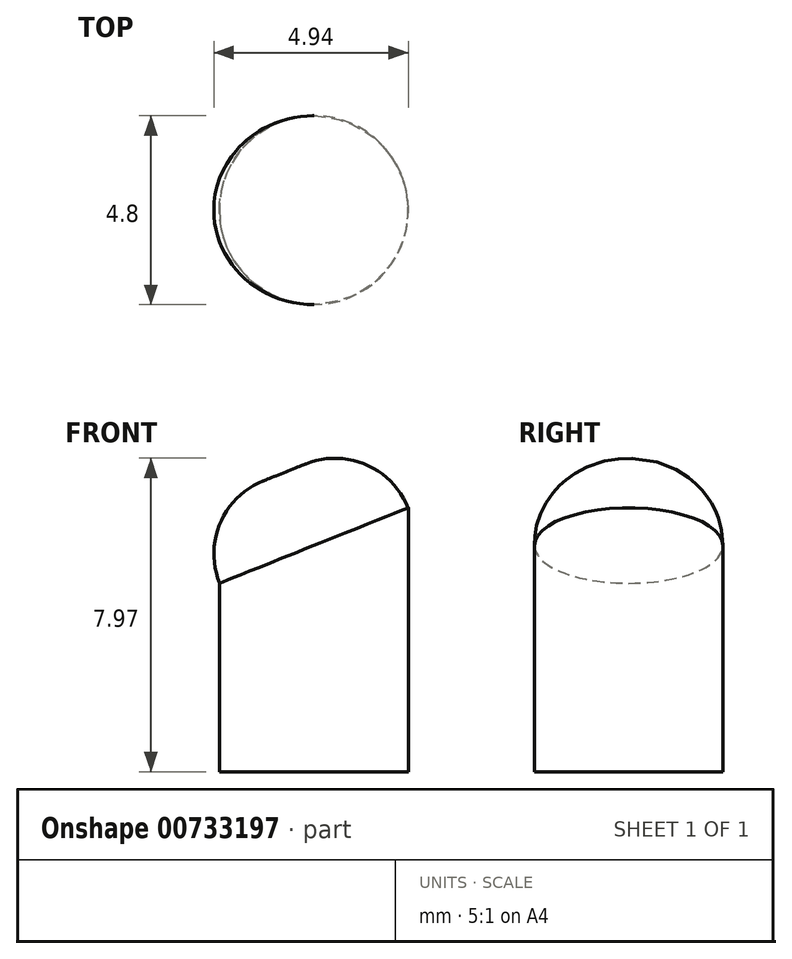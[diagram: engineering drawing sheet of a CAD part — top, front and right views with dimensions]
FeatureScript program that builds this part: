
annotation { "Feature Type Name" : "Feature", "Feature Type Description" : "" }
export const myFeature = defineFeature(function(context is Context, id is Id, definition is map)
    precondition{}
    {
        {
            var Q0;
            Q0=qCreatedBy(makeId("Top.planeOp"),FACE);
            var sketch = newSketch(context, id + "F0", { "sketchPlane" : qUnion([Q0])});
            skCircle(sketch, "E0", {"center": v(0, 0) * mm, "radius": 2.4 * mm});
            skSolve(sketch);
        }
        {
            var Q0;
            Q0=makeQuery(id+"F0.imprint","IMPRINT",FACE,{"disambiguationData":[TD([[makeQuery(id+"F0.imprint","IMPRINT",EDGE,{"derivedFrom":sQuery(id+"F0.wireOp",EDGE,"E0")}),1.0]])]});
            extrude(context, id + "F1", {"entities" : qUnion([Q0]), "depth" : 10 * mm, "offsetDistance" : 25 * mm});
        }
        {
            var Q0;
            Q0=qCreatedBy(makeId("Front.planeOp"),FACE);
            var sketch = newSketch(context, id + "F2", { "sketchPlane" : qUnion([Q0])});
            skLineSegment(sketch, "E1", {"start": v(-2.5, 4.75) * mm, "end": v(2.5, 6.75) * mm});
            skLineSegment(sketch, "E2", {"start": v(-2.5, 4.75) * mm, "end": v(-2.5, 10.5) * mm});
            skLineSegment(sketch, "E3", {"start": v(-2.5, 10.5) * mm, "end": v(2.5, 10.5) * mm});
            skLineSegment(sketch, "E4", {"start": v(2.5, 10.5) * mm, "end": v(2.5, 6.75) * mm});
            skSolve(sketch);
        }
        {
            var Q0;
            {var subQ2=sQuery(id+"F2.wireOp",EDGE,"LqtT72pM-FGjC-ddh8-95cH-kXxwAAOvpNlh");Q0=makeQuery(id+"F2.imprint","IMPRINT",FACE,{"disambiguationData":[TD([[makeQuery(id+"F2.imprint","IMPRINT",EDGE,{"derivedFrom":subQ2}),-1.0]])]});}
            var Q1;
            Q1=makeQuery(id+"F2.imprint","IMPRINT",FACE,{"disambiguationData":[TD([[makeQuery(id+"F2.imprint","IMPRINT",EDGE,{"derivedFrom":sQuery(id+"F2.wireOp",EDGE,"E1")}),1.0]])]});
            extrude(context, id + "F3", {"entities" : qUnion([Q0, Q1]), "operationType" : NewBodyOperationType.REMOVE, "endBound" : BoundingType.SYMMETRIC, "oppositeDirection" : true, "depth" : 8 * mm, "offsetDistance" : 25 * mm});
        }
        {
            var Q0;
            Q0=makeQuery(id+"F3.boolean.opBoolean","COPY",FACE,{"derivedFrom":makeQuery(id+"F3.opExtrude","SWEPT_FACE",FACE,{"disambiguationData":[OSD([sQuery(id+"F2.wireOp",EDGE,"E1")])]})});
            var sketch = newSketch(context, id + "F4", { "sketchPlane" : qUnion([Q0])});
            skEllipse(sketch, "E5", {"center": v(2.14, 0) * mm, "majorRadius": 2.6 * mm, "minorRadius": 2.4 * mm, "majorAxis": v(1, 0)});
            skSolve(sketch);
        }
        {
            var Q0;
            {var subQ0=sQuery(id+"F4.wireOp",EDGE,"E5");var subQ1=makeQuery(id+"F3.boolean.opBoolean","INTERSECT",EDGE,{"derivedFrom":[makeQuery(id+"F1.opExtrude","SWEPT_FACE",FACE,{"disambiguationData":[OSD([sQuery(id+"F0.wireOp",EDGE,"E0")])]}),makeQuery(id+"F3.opExtrude","SWEPT_FACE",FACE,{"disambiguationData":[OSD([sQuery(id+"F2.wireOp",EDGE,"E1")])]})]});var subQ2=makeQuery(id+"F4.imprint","INTERSECT",VERTEX,{"disambiguationData":[OD(0.0)],"derivedFrom":[subQ1,subQ0]});Q0=makeQuery(id+"F4.imprint","IMPRINT",FACE,{"disambiguationData":[TD([[makeQuery(id+"F4.imprint","IMPRINT",EDGE,{"disambiguationData":[TD([[subQ2,-1.0]])],"derivedFrom":subQ1}),-1.0]])]});}
            extrude(context, id + "F5", {"entities" : qUnion([Q0]), "operationType" : NewBodyOperationType.ADD, "depth" : 2 * mm, "offsetDistance" : 25 * mm});
        }
        {
            var Q0;
            Q0=makeQuery(id+"F5.opExtrude","CAP_EDGE",EDGE,{"disambiguationData":[OSD([sQuery(id+"F0.wireOp",EDGE,"E0"),sQuery(id+"F2.wireOp",EDGE,"E1")])],"isStart":false});
            fillet(context, id + "F6", {"entities" : qUnion([Q0]), "radius" : 2 * mm, "tangentPropagation" : true, "allowEdgeOverflow" : false});
        }
    });
